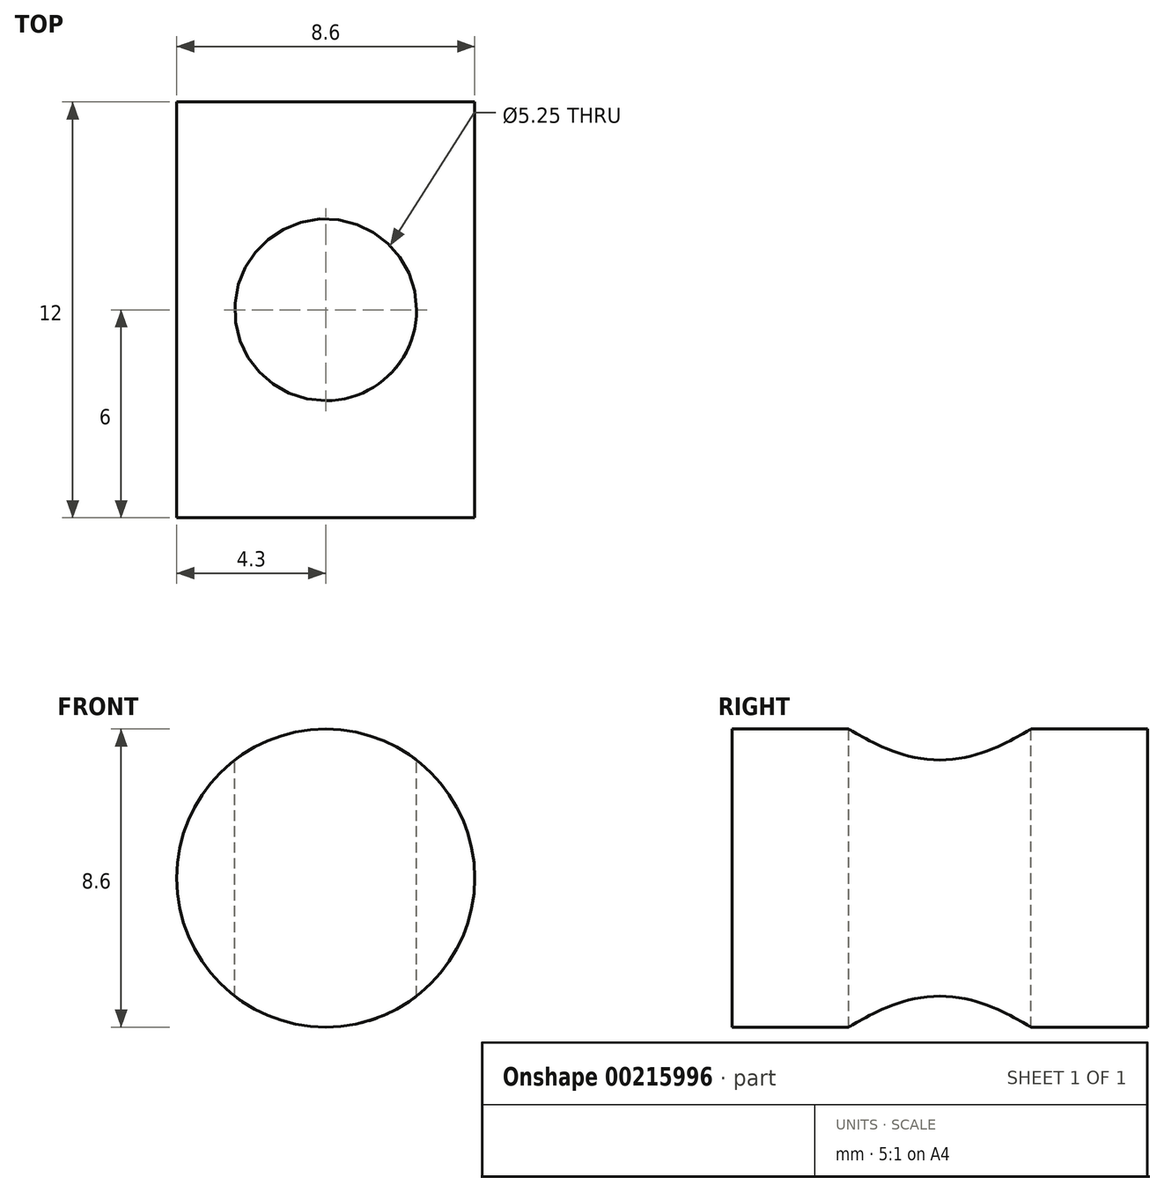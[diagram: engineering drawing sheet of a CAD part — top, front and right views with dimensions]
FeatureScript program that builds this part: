
annotation { "Feature Type Name" : "Feature", "Feature Type Description" : "" }
export const myFeature = defineFeature(function(context is Context, id is Id, definition is map)
    precondition{}
    {
        {
            var Q0;
            Q0=qCreatedBy(makeId("Front.planeOp"),FACE);
            var sketch = newSketch(context, id + "F0", { "sketchPlane" : qUnion([Q0])});
            skCircle(sketch, "E0", {"center": v(0, 0) * mm, "radius": 4.3 * mm});
            skSolve(sketch);
        }
        {
            var Q0;
            Q0=makeQuery(id+"F0.imprint","IMPRINT",FACE,{"disambiguationData":[TD([[makeQuery(id+"F0.imprint","IMPRINT",EDGE,{"derivedFrom":sQuery(id+"F0.wireOp",EDGE,"E0")}),1.0]])]});
            extrude(context, id + "F1", {"entities" : qUnion([Q0]), "endBound" : BoundingType.SYMMETRIC, "depth" : 12 * mm});
        }
        {
            var Q0;
            Q0=qCreatedBy(makeId("Top.planeOp"),FACE);
            cPlane(context, id + "F2", {"entities" : qUnion([Q0]), "cplaneType" : CPlaneType.OFFSET, "offset" : 25 * mm, "width" : 150 * mm, "height" : 150 * mm});
        }
        {
            var Q0;
            Q0=qCreatedBy(id+"F2.planeOp",FACE);
            var sketch = newSketch(context, id + "F3", { "sketchPlane" : qUnion([Q0])});
            skPoint(sketch, "E1", {"position": v(0, 0) * mm});
            skSolve(sketch);
        }
        {
            var Q0;
            Q0=sQuery(id+"F3.wireOp",VERTEX,"E1");
            var Q1;
            Q1=makeQuery(id+"F1.opExtrude","SWEPT_BODY",BODY,{"disambiguationData":[OSD([sQuery(id+"F0.wireOp",EDGE,"E0")])]});
            hole(context, id + "F4", {"style" : HoleStyle.SIMPLE, "endStyle" : HoleEndStyle.THROUGH, "holeDiameter" : 5.25 * mm, "startFromSketch" : true, "locations" : qUnion([Q0]), "scope" : qUnion([Q1]), "isTappedThrough" : true});
        }
    });
